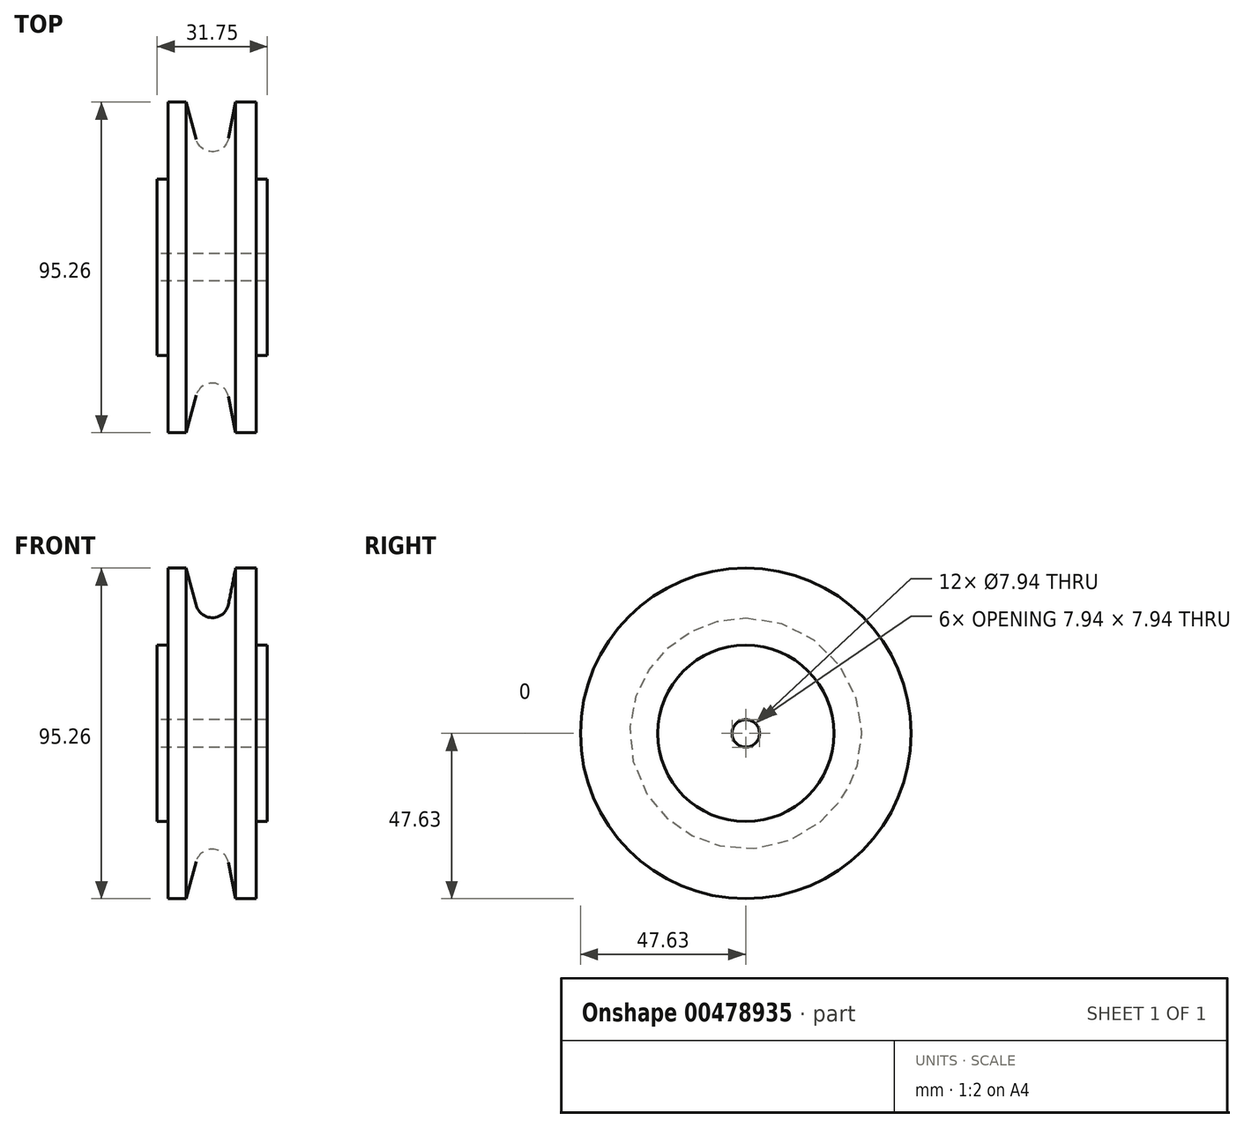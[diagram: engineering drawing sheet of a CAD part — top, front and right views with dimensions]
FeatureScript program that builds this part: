
annotation { "Feature Type Name" : "Feature", "Feature Type Description" : "" }
export const myFeature = defineFeature(function(context is Context, id is Id, definition is map)
    precondition{}
    {
        {
            var Q0;
            Q0=qCreatedBy(makeId("Front.planeOp"),FACE);
            var sketch = newSketch(context, id + "F0", { "sketchPlane" : qUnion([Q0])});
            skLineSegment(sketch, "E0", {"start": v(-59.35, 0) * mm, "end": v(-59.35, 25.4) * mm});
            skLineSegment(sketch, "E1", {"start": v(-59.35, 25.4) * mm, "end": v(-56.18, 25.4) * mm});
            skLineSegment(sketch, "E2", {"start": v(-56.18, 25.4) * mm, "end": v(-56.18, 47.63) * mm});
            skLineSegment(sketch, "E3", {"start": v(-56.18, 47.63) * mm, "end": v(-50.97, 47.63) * mm});
            skLineSegment(sketch, "E4", {"start": v(-30.78, 47.63) * mm, "end": v(-30.78, 25.4) * mm});
            skLineSegment(sketch, "E5", {"start": v(-30.78, 25.4) * mm, "end": v(-27.6, 25.4) * mm});
            skLineSegment(sketch, "E6", {"start": v(-27.6, 25.4) * mm, "end": v(-27.6, 0) * mm});
            skPoint(sketch, "E7.0", {"position": v(0, 0) * mm});
            skArc(sketch, "E8", {"start": v(-48.08, 36.86) * mm, "mid": v(-43.32, 33.34) * mm, "end": v(-38.8, 37.17) * mm});
            skLineSegment(sketch, "E9", {"start": v(-38.8, 37.17) * mm, "end": v(-36.73, 47.63) * mm});
            skLineSegment(sketch, "E10", {"start": v(-48.08, 36.86) * mm, "end": v(-50.97, 47.63) * mm});
            skLineSegment(sketch, "E11.trimOffspring", {"start": v(-36.73, 47.63) * mm, "end": v(-30.78, 47.63) * mm});
            skLineSegment(sketch, "E12", {"start": v(-59.35, 0) * mm, "end": v(-27.6, 0) * mm});
            skSolve(sketch);
        }
        {
            var Q0;
            Q0=makeQuery(id+"F0.imprint","IMPRINT",FACE,{"disambiguationData":[TD([[makeQuery(id+"F0.imprint","IMPRINT",EDGE,{"derivedFrom":sQuery(id+"F0.wireOp",EDGE,"E0")}),-1.0]])]});
            var Q1;
            Q1=sQuery(id+"F0.wireOp",EDGE,"E12");
            revolve(context, id + "F1", {"entities" : qUnion([Q0]), "axis" : qUnion([Q1]), "revolveType" : RevolveType.FULL});
        }
        {
            var Q0;
            Q0=makeQuery(id+"F1.opRevolve","SWEPT_FACE",FACE,{"disambiguationData":[OSD([sQuery(id+"F0.wireOp",EDGE,"E0")])]});
            var sketch = newSketch(context, id + "F2", { "sketchPlane" : qUnion([Q0])});
            skCircle(sketch, "E13", {"center": v(0, 0) * mm, "radius": 3.97 * mm});
            skSolve(sketch);
        }
        {
            var Q0;
            Q0=makeQuery(id+"F2.imprint","IMPRINT",FACE,{"disambiguationData":[TD([[makeQuery(id+"F2.imprint","IMPRINT",EDGE,{"derivedFrom":sQuery(id+"F2.wireOp",EDGE,"E13")}),1.0]])]});
            extrude(context, id + "F3", {"entities" : qUnion([Q0]), "operationType" : NewBodyOperationType.REMOVE, "endBound" : BoundingType.THROUGH_ALL, "oppositeDirection" : true, "depth" : 25.4 * mm, "offsetDistance" : 25.4 * mm});
        }
    });
